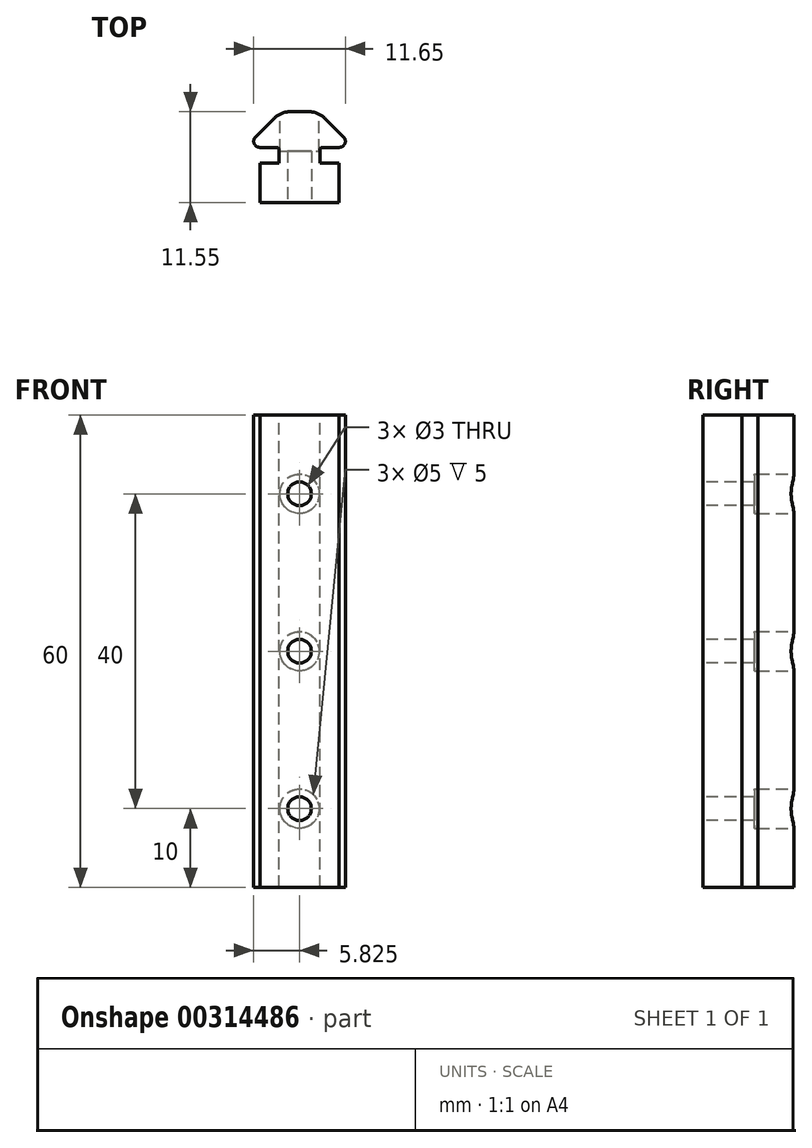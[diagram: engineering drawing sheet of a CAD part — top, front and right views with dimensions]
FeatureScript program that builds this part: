
annotation { "Feature Type Name" : "Feature", "Feature Type Description" : "" }
export const myFeature = defineFeature(function(context is Context, id is Id, definition is map)
    precondition{}
    {
        {
            var Q0;
            Q0=qCreatedBy(makeId("Top.planeOp"),FACE);
            var sketch = newSketch(context, id + "F0", { "sketchPlane" : qUnion([Q0])});
            skLineSegment(sketch, "E0.0.13", {"start": v(-0.8, -19.2) * mm, "end": v(-0.8, -18.5) * mm});
            skArc(sketch, "E0.0.14", {"start": v(-0.8, -18.5) * mm, "mid": v(-0.71, -18.29) * mm, "end": v(-0.5, -18.2) * mm});
            skLineSegment(sketch, "E0.0.15", {"start": v(-0.5, -18.2) * mm, "end": v(1.67, -18.2) * mm});
            skArc(sketch, "E0.0.16", {"start": v(1.67, -18.2) * mm, "mid": v(2.39, -17.72) * mm, "end": v(2.22, -16.87) * mm});
            skLineSegment(sketch, "E0.0.17", {"start": v(2.22, -16.87) * mm, "end": v(-0.12, -14.53) * mm});
            skArc(sketch, "E0.0.18", {"start": v(-0.12, -14.53) * mm, "mid": v(-1.1, -13.88) * mm, "end": v(-2.24, -13.65) * mm});
            skLineSegment(sketch, "E0.0.19", {"start": v(-2.24, -13.65) * mm, "end": v(-4.5, -13.65) * mm});
            skArc(sketch, "E0.0.20", {"start": v(-4.5, -13.65) * mm, "mid": v(-5.66, -13.88) * mm, "end": v(-6.63, -14.53) * mm});
            skLineSegment(sketch, "E0.0.21", {"start": v(-6.63, -14.53) * mm, "end": v(-8.97, -16.87) * mm});
            skArc(sketch, "E0.0.22", {"start": v(-8.97, -16.87) * mm, "mid": v(-9.14, -17.72) * mm, "end": v(-8.42, -18.2) * mm});
            skLineSegment(sketch, "E0.0.23", {"start": v(-8.42, -18.2) * mm, "end": v(-6.25, -18.2) * mm});
            skArc(sketch, "E0.0.24", {"start": v(-6.25, -18.2) * mm, "mid": v(-6.04, -18.29) * mm, "end": v(-5.95, -18.5) * mm});
            skLineSegment(sketch, "E0.0.25", {"start": v(-5.95, -18.5) * mm, "end": v(-5.95, -19.2) * mm});
            skLineSegment(sketch, "E1", {"start": v(-3.38, -13.65) * mm, "end": v(-3.38, -28.6) * mm, "construction": true});
            skLineSegment(sketch, "E2", {"start": v(-5.95, -19.2) * mm, "end": v(-5.95, -20.2) * mm});
            skLineSegment(sketch, "E3", {"start": v(-5.95, -20.2) * mm, "end": v(-8.38, -20.2) * mm});
            skLineSegment(sketch, "E4", {"start": v(-8.38, -20.2) * mm, "end": v(-8.38, -25.2) * mm});
            skLineSegment(sketch, "E5", {"start": v(-8.38, -25.2) * mm, "end": v(-3.38, -25.2) * mm});
            skLineSegment(sketch, "E6.MirrorCS", {"start": v(1.62, -25.2) * mm, "end": v(-3.38, -25.2) * mm});
            skLineSegment(sketch, "E7.MirrorCS", {"start": v(1.62, -20.2) * mm, "end": v(1.62, -25.2) * mm});
            skLineSegment(sketch, "E8.MirrorCS", {"start": v(-0.8, -19.2) * mm, "end": v(-0.8, -20.2) * mm});
            skLineSegment(sketch, "E9.MirrorCS", {"start": v(-0.8, -20.2) * mm, "end": v(1.62, -20.2) * mm});
            skSolve(sketch);
        }
        {
            var Q0;
            Q0 = qSketchRegion(id + "F0", true);
            extrude(context, id + "F1", {"entities" : qUnion([Q0]), "oppositeDirection" : true, "depth" : 60 * mm});
        }
        {
            var Q0;
            Q0=makeQuery(id+"F1.opExtrude","SWEPT_FACE",FACE,{"disambiguationData":[OSD([sQuery(id+"F0.wireOp",EDGE,"E5"),sQuery(id+"F0.wireOp",EDGE,"E6.MirrorCS")])]});
            var sketch = newSketch(context, id + "F2", { "sketchPlane" : qUnion([Q0])});
            skLineSegment(sketch, "E10", {"start": v(-3.38, 0) * mm, "end": v(-3.38, -60) * mm, "construction": true});
            skCircle(sketch, "E11", {"center": v(-3.38, -50) * mm, "radius": 1.5 * mm});
            skCircle(sketch, "E12", {"center": v(-3.38, -30) * mm, "radius": 1.5 * mm});
            skCircle(sketch, "E13", {"center": v(-3.38, -10) * mm, "radius": 1.5 * mm});
            skSolve(sketch);
        }
        {
            var Q0;
            Q0 = qSketchRegion(id + "F2", true);
            extrude(context, id + "F3", {"entities" : qUnion([Q0]), "operationType" : NewBodyOperationType.REMOVE, "oppositeDirection" : true, "depth" : 25 * mm});
        }
        {
            var Q0;
            Q0=makeQuery(id+"F3.boolean.opBoolean","SPLIT",FACE,{"disambiguationData":[TD([makeQuery(id+"F1.opExtrude","SWEPT_FACE",FACE,{"disambiguationData":[OSD([sQuery(id+"F0.wireOp",EDGE,"E0.0.18")])]}),makeQuery(id+"F1.opExtrude","SWEPT_FACE",FACE,{"disambiguationData":[OSD([sQuery(id+"F0.wireOp",EDGE,"E0.0.20")])]}),makeQuery(id+"F3.opExtrude","SWEPT_FACE",FACE,{"disambiguationData":[OSD([sQuery(id+"F2.wireOp",EDGE,"E12")])]}),makeQuery(id+"F3.opExtrude","SWEPT_FACE",FACE,{"disambiguationData":[OSD([sQuery(id+"F2.wireOp",EDGE,"E13")])]})])],"derivedFrom":makeQuery(id+"F1.opExtrude","SWEPT_FACE",FACE,{"disambiguationData":[OSD([sQuery(id+"F0.wireOp",EDGE,"E0.0.19")])]})});
            var sketch = newSketch(context, id + "F4", { "sketchPlane" : qUnion([Q0])});
            skCircle(sketch, "E14", {"center": v(3.38, -10) * mm, "radius": 2.5 * mm});
            skCircle(sketch, "E15", {"center": v(3.38, -30) * mm, "radius": 2.5 * mm});
            skSolve(sketch);
        }
        {
            var Q0;
            {var subQ0=sQuery(id+"F0.wireOp",EDGE,"E0.0.20");var subQ1=sQuery(id+"F0.wireOp",EDGE,"E0.0.19");var subQ2=sQuery(id+"F0.wireOp",EDGE,"E0.0.18");Q0=makeQuery(id+"F3.boolean.opBoolean","SPLIT",FACE,{"disambiguationData":[TD([makeQuery(id+"F1.opExtrude","CAP_FACE",FACE,{"disambiguationData":[OSD([sQuery(id+"F0.wireOp",EDGE,"E0.0.13"),sQuery(id+"F0.wireOp",EDGE,"E0.0.14"),sQuery(id+"F0.wireOp",EDGE,"E0.0.15"),sQuery(id+"F0.wireOp",EDGE,"E0.0.16"),sQuery(id+"F0.wireOp",EDGE,"E0.0.17"),subQ2,subQ1,subQ0,sQuery(id+"F0.wireOp",EDGE,"E0.0.21"),sQuery(id+"F0.wireOp",EDGE,"E0.0.22"),sQuery(id+"F0.wireOp",EDGE,"E0.0.23"),sQuery(id+"F0.wireOp",EDGE,"E0.0.24"),sQuery(id+"F0.wireOp",EDGE,"E0.0.25"),sQuery(id+"F0.wireOp",EDGE,"E2"),sQuery(id+"F0.wireOp",EDGE,"E3"),sQuery(id+"F0.wireOp",EDGE,"E4"),sQuery(id+"F0.wireOp",EDGE,"E5"),sQuery(id+"F0.wireOp",EDGE,"E6.MirrorCS"),sQuery(id+"F0.wireOp",EDGE,"E7.MirrorCS"),sQuery(id+"F0.wireOp",EDGE,"E8.MirrorCS"),sQuery(id+"F0.wireOp",EDGE,"E9.MirrorCS")])],"isStart":false}),makeQuery(id+"F1.opExtrude","SWEPT_FACE",FACE,{"disambiguationData":[OSD([subQ2])]}),makeQuery(id+"F1.opExtrude","SWEPT_FACE",FACE,{"disambiguationData":[OSD([subQ0])]}),makeQuery(id+"F3.opExtrude","SWEPT_FACE",FACE,{"disambiguationData":[OSD([sQuery(id+"F2.wireOp",EDGE,"E11")])]})])],"derivedFrom":makeQuery(id+"F1.opExtrude","SWEPT_FACE",FACE,{"disambiguationData":[OSD([subQ1])]})});}
            var sketch = newSketch(context, id + "F5", { "sketchPlane" : qUnion([Q0])});
            skCircle(sketch, "E16", {"center": v(3.38, -50) * mm, "radius": 2.5 * mm});
            skSolve(sketch);
        }
        {
            var Q0;
            Q0 = qSketchRegion(id + "F4", true);
            var Q1;
            Q1 = qSketchRegion(id + "F5", true);
            extrude(context, id + "F6", {"entities" : qUnion([Q0, Q1]), "operationType" : NewBodyOperationType.REMOVE, "oppositeDirection" : true, "depth" : 5 * mm});
        }
    });
